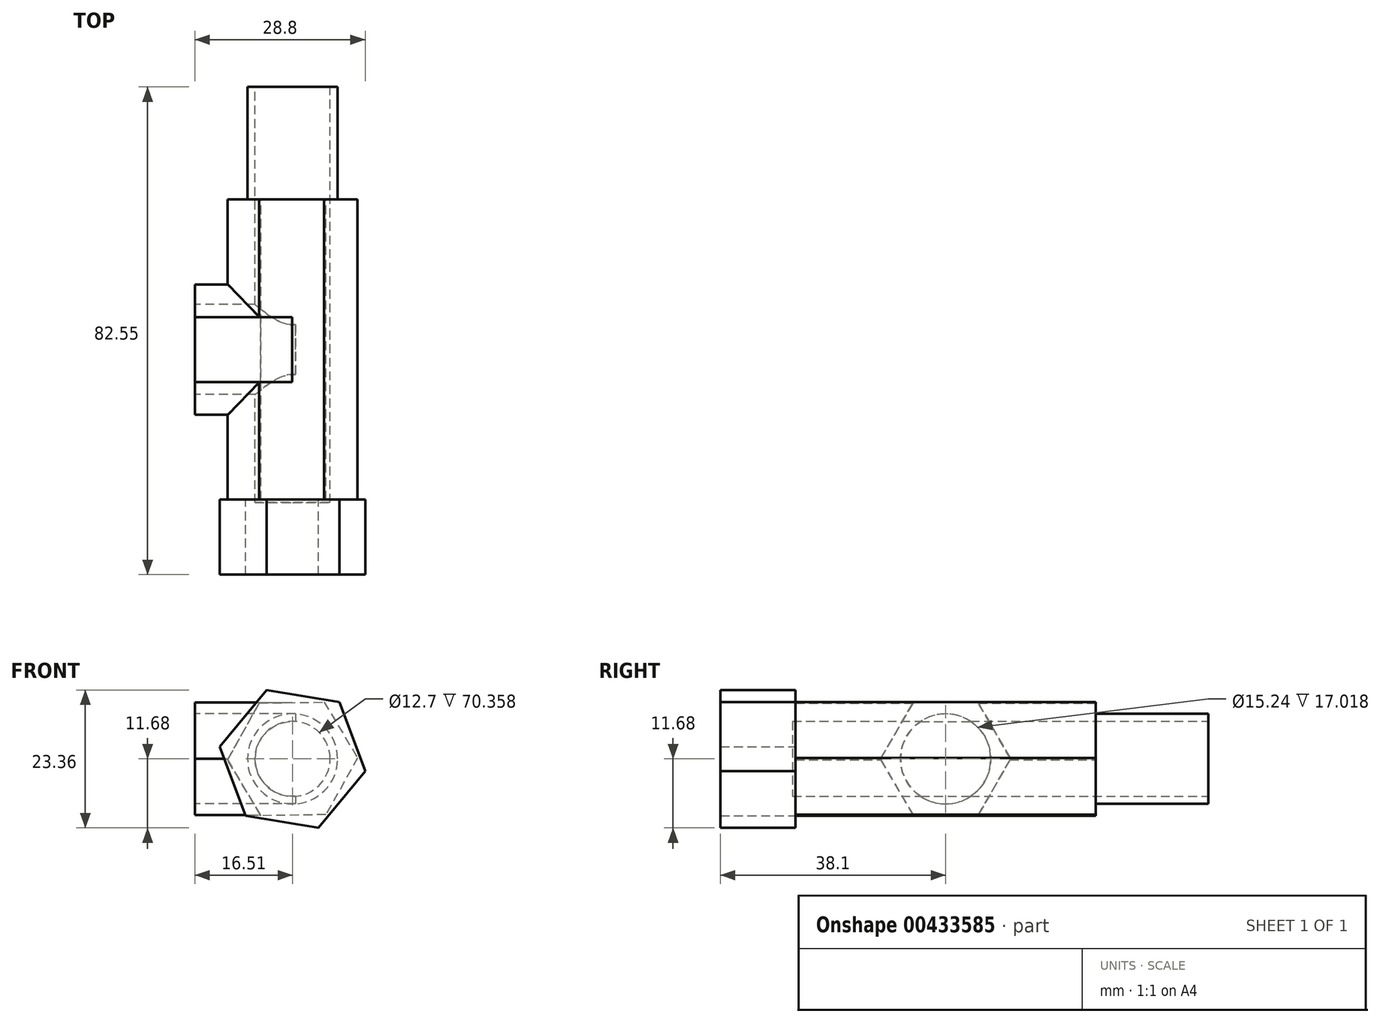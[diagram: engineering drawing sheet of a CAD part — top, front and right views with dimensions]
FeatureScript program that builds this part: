
annotation { "Feature Type Name" : "Feature", "Feature Type Description" : "" }
export const myFeature = defineFeature(function(context is Context, id is Id, definition is map)
    precondition{}
    {
        {
            var Q0;
            Q0=qCreatedBy(makeId("Front.planeOp"),FACE);
            var sketch = newSketch(context, id + "F0", { "sketchPlane" : qUnion([Q0])});
            skCircle(sketch, "E0.cCircle", {"center": v(0, 0) * mm, "radius": 9.53 * mm, "construction": true});
            skLineSegment(sketch, "E0.0", {"start": v(-11, -0.18) * mm, "end": v(-5.65, 9.44) * mm});
            skLineSegment(sketch, "E0.1", {"start": v(-5.65, 9.44) * mm, "end": v(5.35, 9.61) * mm});
            skLineSegment(sketch, "E0.2", {"start": v(5.35, 9.61) * mm, "end": v(11, 0.18) * mm});
            skLineSegment(sketch, "E0.3", {"start": v(11, 0.18) * mm, "end": v(5.65, -9.44) * mm});
            skLineSegment(sketch, "E0.4", {"start": v(5.65, -9.44) * mm, "end": v(-5.35, -9.61) * mm});
            skLineSegment(sketch, "E0.5", {"start": v(-5.35, -9.61) * mm, "end": v(-11, -0.18) * mm});
            skPoint(sketch, "E0.0.midPoint", {"position": v(-8.32, 4.63) * mm});
            skSolve(sketch);
        }
        {
            var Q0;
            Q0=makeQuery(id+"F0.imprint","IMPRINT",FACE,{"disambiguationData":[TD([[makeQuery(id+"F0.imprint","IMPRINT",EDGE,{"derivedFrom":sQuery(id+"F0.wireOp",EDGE,"E0.0")}),-1.0]])]});
            extrude(context, id + "F1", {"entities" : qUnion([Q0]), "depth" : 50.8 * mm});
        }
        {
            var Q0;
            Q0=qCreatedBy(makeId("Right.planeOp"),FACE);
            var sketch = newSketch(context, id + "F2", { "sketchPlane" : qUnion([Q0])});
            skCircle(sketch, "E1.cCircle", {"center": v(-25.4, 0) * mm, "radius": 9.53 * mm, "construction": true});
            skLineSegment(sketch, "E1.0", {"start": v(-30.9, 9.53) * mm, "end": v(-19.9, 9.53) * mm});
            skLineSegment(sketch, "E1.1", {"start": v(-19.9, 9.53) * mm, "end": v(-14.4, 0) * mm});
            skLineSegment(sketch, "E1.2", {"start": v(-14.4, 0) * mm, "end": v(-19.9, -9.53) * mm});
            skLineSegment(sketch, "E1.3", {"start": v(-19.9, -9.53) * mm, "end": v(-30.9, -9.53) * mm});
            skLineSegment(sketch, "E1.4", {"start": v(-30.9, -9.53) * mm, "end": v(-36.4, 0) * mm});
            skLineSegment(sketch, "E1.5", {"start": v(-36.4, 0) * mm, "end": v(-30.9, 9.53) * mm});
            skPoint(sketch, "E1.0.midPoint", {"position": v(-25.4, 9.53) * mm});
            skSolve(sketch);
        }
        {
            var Q0;
            Q0=qSketchRegion(id+"F2",true);
            extrude(context, id + "F3", {"entities" : qUnion([Q0]), "operationType" : NewBodyOperationType.ADD, "oppositeDirection" : true, "depth" : 16.5 * mm});
        }
        {
            var Q0;
            Q0=makeQuery(id+"F1.opExtrude","CAP_FACE",FACE,{"disambiguationData":[OSD([sQuery(id+"F0.wireOp",EDGE,"E0.0"),sQuery(id+"F0.wireOp",EDGE,"E0.1"),sQuery(id+"F0.wireOp",EDGE,"E0.2"),sQuery(id+"F0.wireOp",EDGE,"E0.3"),sQuery(id+"F0.wireOp",EDGE,"E0.4"),sQuery(id+"F0.wireOp",EDGE,"E0.5")])],"isStart":true});
            var sketch = newSketch(context, id + "F4", { "sketchPlane" : qUnion([Q0])});
            skCircle(sketch, "E2", {"center": v(0, 0) * mm, "radius": 7.62 * mm});
            skSolve(sketch);
        }
        {
            var Q0;
            Q0=makeQuery(id+"F1.opExtrude","CAP_FACE",FACE,{"disambiguationData":[OSD([sQuery(id+"F0.wireOp",EDGE,"E0.0"),sQuery(id+"F0.wireOp",EDGE,"E0.1"),sQuery(id+"F0.wireOp",EDGE,"E0.2"),sQuery(id+"F0.wireOp",EDGE,"E0.3"),sQuery(id+"F0.wireOp",EDGE,"E0.4"),sQuery(id+"F0.wireOp",EDGE,"E0.5")])],"isStart":false});
            var sketch = newSketch(context, id + "F5", { "sketchPlane" : qUnion([Q0])});
            skCircle(sketch, "E3.cCircle", {"center": v(0, 0) * mm, "radius": 10.8 * mm, "construction": true});
            skPoint(sketch, "E3.cCircle.perimeterSnap0", {"position": v(-8.32, 4.63) * mm});
            skLineSegment(sketch, "E3.0", {"start": v(-12.3, 2.07) * mm, "end": v(-4.36, 11.68) * mm});
            skLineSegment(sketch, "E3.1", {"start": v(-4.36, 11.68) * mm, "end": v(7.94, 9.61) * mm});
            skLineSegment(sketch, "E3.2", {"start": v(7.94, 9.61) * mm, "end": v(12.3, -2.07) * mm});
            skLineSegment(sketch, "E3.3", {"start": v(12.3, -2.07) * mm, "end": v(4.36, -11.68) * mm});
            skLineSegment(sketch, "E3.4", {"start": v(4.36, -11.68) * mm, "end": v(-7.94, -9.61) * mm});
            skLineSegment(sketch, "E3.5", {"start": v(-7.94, -9.61) * mm, "end": v(-12.3, 2.07) * mm});
            skPoint(sketch, "E3.0.midPoint", {"position": v(-8.32, 6.87) * mm});
            skPoint(sketch, "E3.0.midPoint.positionSnap0", {"position": v(-8.32, 4.63) * mm});
            skSolve(sketch);
        }
        {
            var Q0;
            Q0=qSketchRegion(id+"F5",true);
            extrude(context, id + "F6", {"entities" : qUnion([Q0]), "operationType" : NewBodyOperationType.ADD, "depth" : 12.7 * mm});
        }
        {
            var Q0;
            Q0=makeQuery(id+"F4.imprint","IMPRINT",FACE,{"disambiguationData":[TD([[makeQuery(id+"F4.imprint","IMPRINT",EDGE,{"derivedFrom":sQuery(id+"F4.wireOp",EDGE,"E2")}),1.0]])]});
            extrude(context, id + "F7", {"entities" : qUnion([Q0]), "operationType" : NewBodyOperationType.ADD, "depth" : 19.05 * mm});
        }
        {
            var Q0;
            Q0=makeQuery(id+"F7.opExtrude","CAP_FACE",FACE,{"disambiguationData":[OSD([sQuery(id+"F4.wireOp",EDGE,"E2")])],"isStart":false});
            var sketch = newSketch(context, id + "F8", { "sketchPlane" : qUnion([Q0])});
            skCircle(sketch, "E4", {"center": v(0, 0) * mm, "radius": 6.35 * mm});
            skSolve(sketch);
        }
        {
            var Q0;
            Q0=makeQuery(id+"F8.imprint","IMPRINT",FACE,{"disambiguationData":[TD([[makeQuery(id+"F8.imprint","IMPRINT",EDGE,{"derivedFrom":sQuery(id+"F8.wireOp",EDGE,"E4")}),1.0]])]});
            extrude(context, id + "F9", {"entities" : qUnion([Q0]), "operationType" : NewBodyOperationType.REMOVE, "oppositeDirection" : true, "depth" : 70.36 * mm});
        }
        {
            var Q0;
            Q0=makeQuery(id+"F3.opExtrude","CAP_FACE",FACE,{"disambiguationData":[OSD([sQuery(id+"F2.wireOp",EDGE,"E1.0"),sQuery(id+"F2.wireOp",EDGE,"E1.1"),sQuery(id+"F2.wireOp",EDGE,"E1.2"),sQuery(id+"F2.wireOp",EDGE,"E1.3"),sQuery(id+"F2.wireOp",EDGE,"E1.4"),sQuery(id+"F2.wireOp",EDGE,"E1.5")])],"isStart":false});
            var sketch = newSketch(context, id + "F10", { "sketchPlane" : qUnion([Q0])});
            skCircle(sketch, "E5", {"center": v(25.4, 0) * mm, "radius": 7.62 * mm});
            skPoint(sketch, "E5.centerSnap0", {"position": v(25.4, 9.53) * mm});
            skPoint(sketch, "E5.perimeterSnap0", {"position": v(25.4, 9.53) * mm});
            skPoint(sketch, "E5.perimeterSnap1", {"position": v(33.65, 4.76) * mm});
            skSolve(sketch);
        }
        {
            var Q0;
            Q0=makeQuery(id+"F10.imprint","IMPRINT",FACE,{"disambiguationData":[TD([[makeQuery(id+"F10.imprint","IMPRINT",EDGE,{"derivedFrom":sQuery(id+"F10.wireOp",EDGE,"E5")}),1.0]])]});
            extrude(context, id + "F11", {"entities" : qUnion([Q0]), "operationType" : NewBodyOperationType.REMOVE, "oppositeDirection" : true, "depth" : 17.02 * mm});
        }
    });
